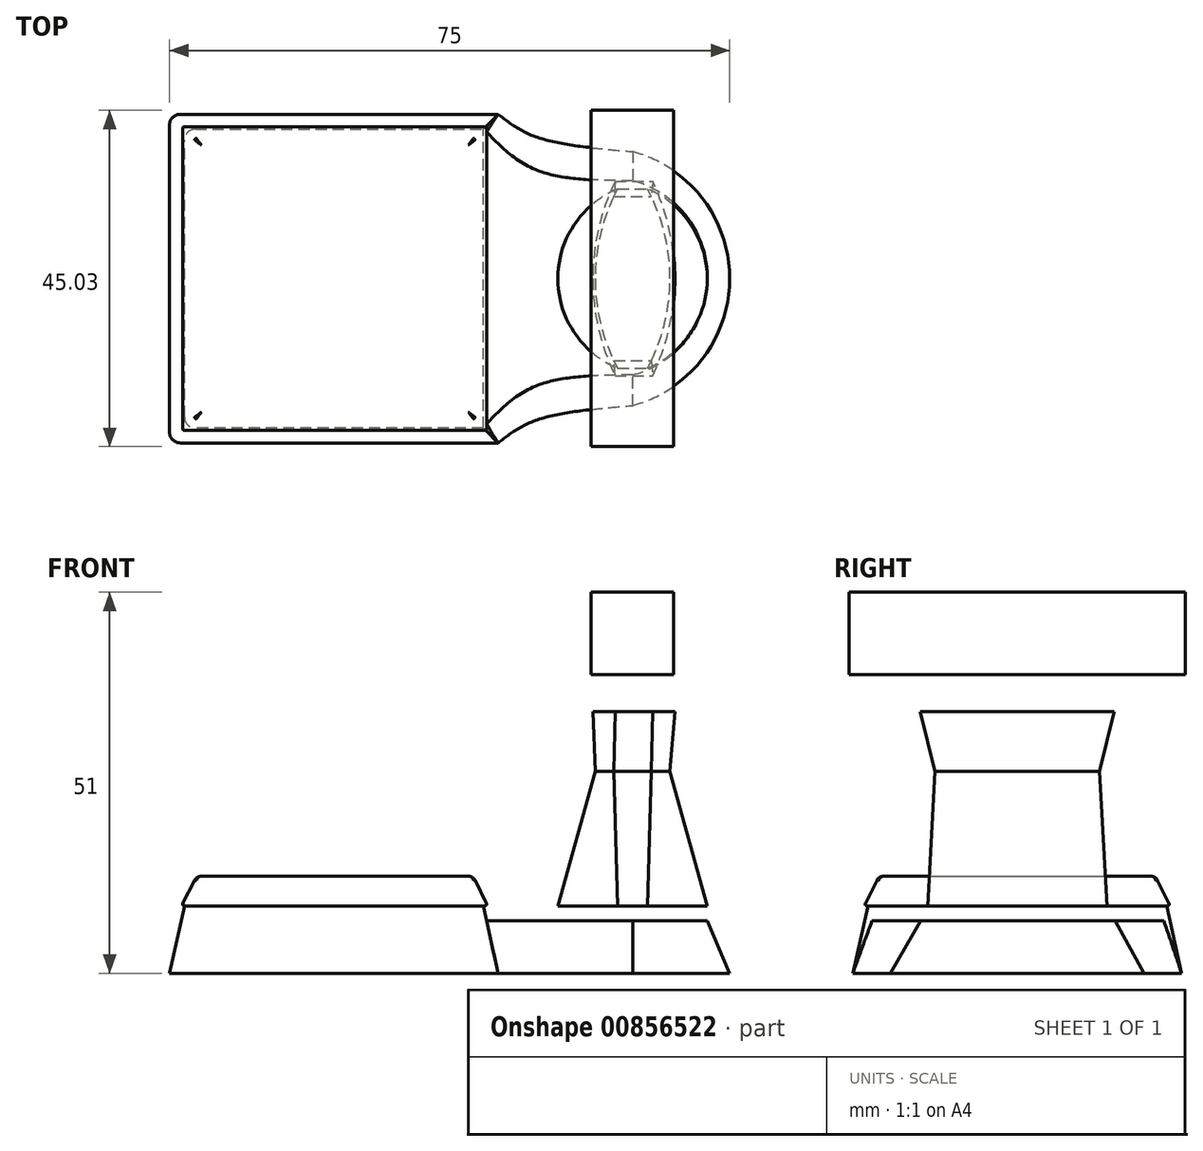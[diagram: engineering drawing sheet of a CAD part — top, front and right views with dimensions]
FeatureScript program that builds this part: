
annotation { "Feature Type Name" : "Feature", "Feature Type Description" : "" }
export const myFeature = defineFeature(function(context is Context, id is Id, definition is map)
    precondition{}
    {
        {
            var Q0;
            Q0=qCreatedBy(makeId("Top.planeOp"),FACE);
            var sketch = newSketch(context, id + "F0", { "sketchPlane" : qUnion([Q0])});
            skLineSegment(sketch, "E0.bottom", {"start": v(0, 0) * mm, "end": v(44, 0) * mm});
            skLineSegment(sketch, "E0.top", {"start": v(0, 44) * mm, "end": v(44, 44) * mm});
            skLineSegment(sketch, "E0.left", {"start": v(0, 0) * mm, "end": v(0, 44) * mm});
            skLineSegment(sketch, "E1", {"start": v(75, 22) * mm, "end": v(62, 22) * mm});
            skLineSegment(sketch, "E2", {"start": v(62, 22) * mm, "end": v(62, 39) * mm});
            skLineSegment(sketch, "E3", {"start": v(62, 22) * mm, "end": v(62, 5) * mm});
            skArc(sketch, "E4", {"start": v(62, 5) * mm, "mid": v(75, 22) * mm, "end": v(62, 39) * mm});
            skFitSpline(sketch, "E5", {"points": [v(44, 44) * mm, v(49, 41) * mm, v(62, 39) * mm], "startDerivative": vector(10.68, -8.34) * mm, "endDerivative": vector(24.4, -2.08) * mm});
            skFitSpline(sketch, "E6", {"points": [v(44, 0) * mm, v(49, 3) * mm, v(62, 5) * mm], "startDerivative": vector(10.68, 8.34) * mm, "endDerivative": vector(24.4, 2.08) * mm});
            skLineSegment(sketch, "E7", {"start": v(44, 0) * mm, "end": v(44, 44) * mm});
            skLineSegment(sketch, "E8", {"start": v(49, 41) * mm, "end": v(49, 3) * mm});
            skSolve(sketch);
        }
        {
            var Q0;
            Q0=qCreatedBy(makeId("Top.planeOp"),FACE);
            cPlane(context, id + "F1", {"entities" : qUnion([Q0]), "cplaneType" : CPlaneType.OFFSET, "offset" : 9 * mm, "width" : 150 * mm, "height" : 150 * mm});
        }
        {
            var Q0;
            Q0=qCreatedBy(id+"F1.planeOp",FACE);
            var sketch = newSketch(context, id + "F2", { "sketchPlane" : qUnion([Q0])});
            skLineSegment(sketch, "E9.top", {"start": v(2, 42) * mm, "end": v(42, 42) * mm});
            skLineSegment(sketch, "E9.left", {"start": v(2, 2) * mm, "end": v(2, 42) * mm});
            skLineSegment(sketch, "E9.right", {"start": v(42, 2) * mm, "end": v(42, 42) * mm});
            skLineSegment(sketch, "E10", {"start": v(62, 22) * mm, "end": v(62, 9) * mm});
            skLineSegment(sketch, "E11", {"start": v(62, 22) * mm, "end": v(72, 22) * mm});
            skLineSegment(sketch, "E12", {"start": v(42, 2) * mm, "end": v(2, 2) * mm});
            skLineSegment(sketch, "E13", {"start": v(49, 36.5) * mm, "end": v(49, 7.5) * mm});
            skLineSegment(sketch, "E14", {"start": v(62, 22) * mm, "end": v(62, 34) * mm});
            skLineSegment(sketch, "E15", {"start": v(62, 22) * mm, "end": v(62, 10) * mm});
            skLineSegment(sketch, "E16", {"start": v(62, 34) * mm, "end": v(64, 34) * mm});
            skLineSegment(sketch, "E17", {"start": v(62, 10) * mm, "end": v(64, 10) * mm});
            skArc(sketch, "E18", {"start": v(64, 10) * mm, "mid": v(72, 22) * mm, "end": v(64, 34) * mm});
            skLineSegment(sketch, "E19", {"start": v(62, 34) * mm, "end": v(60, 34) * mm});
            skLineSegment(sketch, "E20", {"start": v(62, 10) * mm, "end": v(60, 10) * mm});
            skArc(sketch, "E21", {"start": v(60, 34) * mm, "mid": v(52, 22) * mm, "end": v(60, 10) * mm});
            skLineSegment(sketch, "E22", {"start": v(62, 22) * mm, "end": v(52, 22) * mm});
            skSolve(sketch);
        }
        {
            var Q0;
            Q0=makeQuery(id+"F2.imprint","IMPRINT",FACE,{"disambiguationData":[TD([[makeQuery(id+"F2.imprint","IMPRINT",EDGE,{"derivedFrom":sQuery(id+"F2.wireOp",EDGE,"E9.top")}),-1.0]])]});
            var Q1;
            Q1=makeQuery(id+"F0.imprint","IMPRINT",FACE,{"disambiguationData":[TD([[makeQuery(id+"F0.imprint","IMPRINT",EDGE,{"derivedFrom":sQuery(id+"F0.wireOp",EDGE,"E0.bottom")}),1.0]])]});
            loft(context, id + "F3", {"sheetProfilesArray" : [{ "sheetProfileEntities" : qUnion([Q0]) }, { "sheetProfileEntities" : qUnion([Q1]) }]});
        }
        {
            var Q0;
            Q0=makeQuery(id+"F3.opLoft","SWEPT_EDGE",EDGE,{"disambiguationData":[OSD([sQuery(id+"F0.wireOp",EDGE,"E0.bottom"),sQuery(id+"F0.wireOp",EDGE,"E0.left"),sQuery(id+"F2.wireOp",EDGE,"E9.left"),sQuery(id+"F2.wireOp",EDGE,"E12")])]});
            fillet(context, id + "F4", {"entities" : qUnion([Q0]), "radius" : 1.5 * mm, "tangentPropagation" : true, "allowEdgeOverflow" : false});
        }
        {
            var Q0;
            Q0=makeQuery(id+"F3.opLoft","SWEPT_EDGE",EDGE,{"disambiguationData":[OSD([sQuery(id+"F0.wireOp",EDGE,"E0.top"),sQuery(id+"F0.wireOp",EDGE,"E0.left"),sQuery(id+"F2.wireOp",EDGE,"E9.top"),sQuery(id+"F2.wireOp",EDGE,"E9.left")])]});
            fillet(context, id + "F5", {"entities" : qUnion([Q0]), "radius" : 1.5 * mm, "tangentPropagation" : true, "allowEdgeOverflow" : false});
        }
        {
            var Q0;
            Q0=qCreatedBy(id+"F1.planeOp",FACE);
            var sketch = newSketch(context, id + "F6", { "sketchPlane" : qUnion([Q0])});
            skLineSegment(sketch, "E23.bottom", {"start": v(0.1, 0) * mm, "end": v(1.6, 0) * mm});
            skLineSegment(sketch, "E23.top", {"start": v(0.1, 1.5) * mm, "end": v(1.6, 1.5) * mm});
            skLineSegment(sketch, "E23.left", {"start": v(0.1, 0) * mm, "end": v(0.1, 1.5) * mm});
            skLineSegment(sketch, "E23.right", {"start": v(1.6, 0) * mm, "end": v(1.6, 1.5) * mm});
            skLineSegment(sketch, "E24.bottom", {"start": v(1.6, 1.5) * mm, "end": v(42.6, 1.5) * mm});
            skLineSegment(sketch, "E24.top", {"start": v(1.6, 42.5) * mm, "end": v(42.6, 42.5) * mm});
            skLineSegment(sketch, "E24.left", {"start": v(1.6, 1.5) * mm, "end": v(1.6, 42.5) * mm});
            skLineSegment(sketch, "E24.right", {"start": v(42.6, 1.5) * mm, "end": v(42.6, 42.5) * mm});
            skSolve(sketch);
        }
        {
            var Q0;
            Q0=qCreatedBy(id+"F1.planeOp",FACE);
            cPlane(context, id + "F7", {"entities" : qUnion([Q0]), "cplaneType" : CPlaneType.OFFSET, "offset" : 4 * mm, "width" : 150 * mm, "height" : 150 * mm});
        }
        {
            var Q0;
            Q0=qCreatedBy(id+"F7.planeOp",FACE);
            var sketch = newSketch(context, id + "F8", { "sketchPlane" : qUnion([Q0])});
            skLineSegment(sketch, "E25.bottom", {"start": v(0.15, 0) * mm, "end": v(3.65, 0) * mm});
            skLineSegment(sketch, "E25.top", {"start": v(0.15, 3.5) * mm, "end": v(3.65, 3.5) * mm});
            skLineSegment(sketch, "E25.left", {"start": v(0.15, 0) * mm, "end": v(0.15, 3.5) * mm});
            skLineSegment(sketch, "E25.right", {"start": v(3.65, 0) * mm, "end": v(3.65, 3.5) * mm});
            skLineSegment(sketch, "E26.bottom", {"start": v(3.65, 3.5) * mm, "end": v(40.65, 3.5) * mm});
            skLineSegment(sketch, "E26.top", {"start": v(3.65, 40.5) * mm, "end": v(40.65, 40.5) * mm});
            skLineSegment(sketch, "E26.left", {"start": v(3.65, 3.5) * mm, "end": v(3.65, 40.5) * mm});
            skLineSegment(sketch, "E26.right", {"start": v(40.65, 3.5) * mm, "end": v(40.65, 40.5) * mm});
            skSolve(sketch);
        }
        {
            var Q0;
            Q0=makeQuery(id+"F6.imprint","IMPRINT",FACE,{"disambiguationData":[TD([[makeQuery(id+"F6.imprint","IMPRINT",EDGE,{"derivedFrom":sQuery(id+"F6.wireOp",EDGE,"E24.bottom")}),1.0]])]});
            var Q1;
            Q1=makeQuery(id+"F8.imprint","IMPRINT",FACE,{"disambiguationData":[TD([[makeQuery(id+"F8.imprint","IMPRINT",EDGE,{"derivedFrom":sQuery(id+"F8.wireOp",EDGE,"E26.bottom")}),1.0]])]});
            loft(context, id + "F9", {"sheetProfilesArray" : [{ "sheetProfileEntities" : qUnion([Q0]) }, { "sheetProfileEntities" : qUnion([Q1]) }]});
        }
        {
            var Q0;
            Q0=makeQuery(id+"F9.opLoft","MID_CAP_EDGE",EDGE,{"disambiguationData":[OSD([sQuery(id+"F8.wireOp",EDGE,"E25.top"),sQuery(id+"F8.wireOp",EDGE,"E25.right"),sQuery(id+"F8.wireOp",EDGE,"E26.bottom"),sQuery(id+"F8.wireOp",EDGE,"E26.left"),sQuery(id+"F8.wireOp",EDGE,"E26.right")])],"capPos":1.0});
            var Q1;
            Q1=makeQuery(id+"F9.opLoft","MID_CAP_EDGE",EDGE,{"disambiguationData":[OSD([sQuery(id+"F8.wireOp",EDGE,"E25.top"),sQuery(id+"F8.wireOp",EDGE,"E25.right"),sQuery(id+"F8.wireOp",EDGE,"E26.bottom"),sQuery(id+"F8.wireOp",EDGE,"E26.top"),sQuery(id+"F8.wireOp",EDGE,"E26.left")])],"capPos":1.0});
            var Q2;
            Q2=makeQuery(id+"F9.opLoft","CAP_FACE",FACE,{"disambiguationData":[OSD([makeQuery(id+"F8.imprint","IMPRINT",FACE,{"disambiguationData":[TD([[makeQuery(id+"F8.imprint","IMPRINT",EDGE,{"derivedFrom":sQuery(id+"F8.wireOp",EDGE,"E26.bottom")}),1.0]])]})])],"isStart":true});
            fillet(context, id + "F10", {"entities" : qUnion([Q0, Q1, Q2]), "radius" : 1 * mm, "tangentPropagation" : true, "allowEdgeOverflow" : false});
        }
        {
            var Q0;
            Q0=makeQuery(id+"F9.opLoft","SWEPT_FACE",FACE,{"disambiguationData":[OSD([sQuery(id+"F6.wireOp",EDGE,"E23.top"),sQuery(id+"F6.wireOp",EDGE,"E23.right"),sQuery(id+"F6.wireOp",EDGE,"E24.bottom"),sQuery(id+"F6.wireOp",EDGE,"E24.left"),sQuery(id+"F6.wireOp",EDGE,"E24.right"),sQuery(id+"F8.wireOp",EDGE,"E25.top"),sQuery(id+"F8.wireOp",EDGE,"E25.right"),sQuery(id+"F8.wireOp",EDGE,"E26.bottom"),sQuery(id+"F8.wireOp",EDGE,"E26.left"),sQuery(id+"F8.wireOp",EDGE,"E26.right")])]});
            var Q1;
            Q1=makeQuery(id+"F9.opLoft","SWEPT_FACE",FACE,{"disambiguationData":[OSD([sQuery(id+"F6.wireOp",EDGE,"E23.top"),sQuery(id+"F6.wireOp",EDGE,"E23.right"),sQuery(id+"F6.wireOp",EDGE,"E24.bottom"),sQuery(id+"F6.wireOp",EDGE,"E24.top"),sQuery(id+"F6.wireOp",EDGE,"E24.left"),sQuery(id+"F8.wireOp",EDGE,"E25.top"),sQuery(id+"F8.wireOp",EDGE,"E25.right"),sQuery(id+"F8.wireOp",EDGE,"E26.bottom"),sQuery(id+"F8.wireOp",EDGE,"E26.top"),sQuery(id+"F8.wireOp",EDGE,"E26.left")])]});
            var Q2;
            Q2=makeQuery(id+"F9.opLoft","SWEPT_FACE",FACE,{"disambiguationData":[OSD([sQuery(id+"F6.wireOp",EDGE,"E24.bottom"),sQuery(id+"F6.wireOp",EDGE,"E24.top"),sQuery(id+"F6.wireOp",EDGE,"E24.right"),sQuery(id+"F8.wireOp",EDGE,"E26.bottom"),sQuery(id+"F8.wireOp",EDGE,"E26.top"),sQuery(id+"F8.wireOp",EDGE,"E26.right")])]});
            var Q3;
            Q3=makeQuery(id+"F9.opLoft","SWEPT_FACE",FACE,{"disambiguationData":[OSD([sQuery(id+"F6.wireOp",EDGE,"E24.top"),sQuery(id+"F6.wireOp",EDGE,"E24.left"),sQuery(id+"F6.wireOp",EDGE,"E24.right"),sQuery(id+"F8.wireOp",EDGE,"E26.top"),sQuery(id+"F8.wireOp",EDGE,"E26.left"),sQuery(id+"F8.wireOp",EDGE,"E26.right")])]});
            fillet(context, id + "F11", {"entities" : qUnion([Q0, Q1, Q2, Q3]), "radius" : 0.25 * mm, "tangentPropagation" : true, "allowEdgeOverflow" : false});
        }
        {
            var Q0;
            Q0=qCreatedBy(makeId("Top.planeOp"),FACE);
            cPlane(context, id + "F12", {"entities" : qUnion([Q0]), "cplaneType" : CPlaneType.OFFSET, "offset" : 40 * mm, "width" : 150 * mm, "height" : 150 * mm});
        }
        {
            var Q0;
            Q0=qCreatedBy(id+"F12.planeOp",FACE);
            var sketch = newSketch(context, id + "F13", { "sketchPlane" : qUnion([Q0])});
            skLineSegment(sketch, "E27.bottom", {"start": v(56.47, 44.53) * mm, "end": v(67.47, 44.53) * mm});
            skLineSegment(sketch, "E27.top", {"start": v(56.47, -0.5) * mm, "end": v(67.47, -0.5) * mm});
            skLineSegment(sketch, "E28", {"start": v(56.47, 44.53) * mm, "end": v(56.47, -0.5) * mm});
            skLineSegment(sketch, "E29", {"start": v(67.47, 44.53) * mm, "end": v(67.47, -0.5) * mm});
            skSolve(sketch);
        }
        {
            var Q0;
            Q0=makeQuery(id+"F13.imprint","IMPRINT",FACE,{"disambiguationData":[TD([[makeQuery(id+"F13.imprint","IMPRINT",EDGE,{"derivedFrom":sQuery(id+"F13.wireOp",EDGE,"E27.bottom")}),-1.0]])]});
            extrude(context, id + "F14", {"entities" : qUnion([Q0]), "depth" : 11 * mm, "offsetDistance" : 25 * mm});
        }
        {
            var Q0;
            Q0=qCreatedBy(makeId("Top.planeOp"),FACE);
            cPlane(context, id + "F15", {"entities" : qUnion([Q0]), "cplaneType" : CPlaneType.OFFSET, "offset" : 27 * mm, "width" : 150 * mm, "height" : 150 * mm});
        }
        {
            var Q0;
            Q0=qCreatedBy(makeId("Top.planeOp"),FACE);
            cPlane(context, id + "F16", {"entities" : qUnion([Q0]), "cplaneType" : CPlaneType.OFFSET, "offset" : 35 * mm, "width" : 150 * mm, "height" : 150 * mm});
        }
        {
            var Q0;
            Q0=qCreatedBy(id+"F15.planeOp",FACE);
            var sketch = newSketch(context, id + "F17", { "sketchPlane" : qUnion([Q0])});
            skLineSegment(sketch, "E30", {"start": v(67, 22) * mm, "end": v(62, 22) * mm});
            skLineSegment(sketch, "E31", {"start": v(62, 22) * mm, "end": v(62, 33) * mm});
            skLineSegment(sketch, "E32", {"start": v(62, 22) * mm, "end": v(62, 11) * mm});
            skLineSegment(sketch, "E33", {"start": v(62, 22) * mm, "end": v(57, 22) * mm});
            skLineSegment(sketch, "E34", {"start": v(62, 33) * mm, "end": v(64.5, 33) * mm});
            skLineSegment(sketch, "E35", {"start": v(62, 33) * mm, "end": v(59.5, 33) * mm});
            skLineSegment(sketch, "E36", {"start": v(62, 11) * mm, "end": v(64.5, 11) * mm});
            skLineSegment(sketch, "E37", {"start": v(62, 11) * mm, "end": v(59.5, 11) * mm});
            skArc(sketch, "E38", {"start": v(64.5, 11) * mm, "mid": v(67, 22) * mm, "end": v(64.5, 33) * mm});
            skArc(sketch, "E39", {"start": v(59.5, 33) * mm, "mid": v(57, 22) * mm, "end": v(59.5, 11) * mm});
            skSolve(sketch);
        }
        {
            var Q0;
            Q0=qCreatedBy(id+"F16.planeOp",FACE);
            var sketch = newSketch(context, id + "F18", { "sketchPlane" : qUnion([Q0])});
            skLineSegment(sketch, "E40", {"start": v(62.17, 22) * mm, "end": v(62.17, 35) * mm});
            skLineSegment(sketch, "E41", {"start": v(62.17, 22) * mm, "end": v(62.17, 9) * mm});
            skLineSegment(sketch, "E42", {"start": v(62.17, 35) * mm, "end": v(64.67, 35) * mm});
            skLineSegment(sketch, "E43", {"start": v(62.17, 35) * mm, "end": v(59.67, 35) * mm});
            skLineSegment(sketch, "E44", {"start": v(62.17, 9) * mm, "end": v(64.67, 9) * mm});
            skLineSegment(sketch, "E45", {"start": v(62.17, 9) * mm, "end": v(59.67, 9) * mm});
            skLineSegment(sketch, "E46", {"start": v(62.17, 22) * mm, "end": v(67.67, 22) * mm});
            skLineSegment(sketch, "E47", {"start": v(67.67, 22) * mm, "end": v(62.17, 22) * mm});
            skLineSegment(sketch, "E48", {"start": v(62.17, 22) * mm, "end": v(56.67, 22) * mm});
            skArc(sketch, "E49", {"start": v(64.67, 9) * mm, "mid": v(67.67, 22) * mm, "end": v(64.67, 35) * mm});
            skArc(sketch, "E50", {"start": v(59.67, 35) * mm, "mid": v(56.67, 22) * mm, "end": v(59.67, 9) * mm});
            skSolve(sketch);
        }
        {
            var Q0;
            Q0=qCreatedBy(makeId("Top.planeOp"),FACE);
            cPlane(context, id + "F19", {"entities" : qUnion([Q0]), "cplaneType" : CPlaneType.OFFSET, "offset" : 7 * mm, "width" : 150 * mm, "height" : 150 * mm});
        }
        {
            var Q0;
            Q0=qCreatedBy(id+"F19.planeOp",FACE);
            var sketch = newSketch(context, id + "F20", { "sketchPlane" : qUnion([Q0])});
            skLineSegment(sketch, "E51.top", {"start": v(2, 42.1) * mm, "end": v(42, 42.1) * mm});
            skLineSegment(sketch, "E51.left", {"start": v(2, 2.1) * mm, "end": v(2, 42.1) * mm});
            skLineSegment(sketch, "E51.right", {"start": v(42, 2.1) * mm, "end": v(42, 42.1) * mm});
            skLineSegment(sketch, "E52", {"start": v(62, 22.1) * mm, "end": v(62, 35.1) * mm});
            skLineSegment(sketch, "E53", {"start": v(62, 22.1) * mm, "end": v(62, 9.1) * mm});
            skLineSegment(sketch, "E54", {"start": v(62, 22.1) * mm, "end": v(72, 22.1) * mm});
            skArc(sketch, "E55", {"start": v(62, 9.1) * mm, "mid": v(72, 22.1) * mm, "end": v(62, 35.1) * mm});
            skLineSegment(sketch, "E56", {"start": v(42, 2.1) * mm, "end": v(2, 2.1) * mm});
            skLineSegment(sketch, "E57", {"start": v(49, 36.6) * mm, "end": v(49, 7.6) * mm});
            skFitSpline(sketch, "E58", {"points": [v(62, 35.1) * mm, v(49, 36.6) * mm, v(42, 42.1) * mm], "startDerivative": vector(-25.98, 0.15) * mm, "endDerivative": vector(-13.63, 14.3) * mm});
            skFitSpline(sketch, "E59", {"points": [v(62, 9.1) * mm, v(49, 7.6) * mm, v(42, 2.1) * mm], "startDerivative": vector(-25.98, -0.15) * mm, "endDerivative": vector(-13.63, -14.3) * mm});
            skSolve(sketch);
        }
        {
            var Q0;
            {var subQ0=sQuery(id+"F17.wireOp",EDGE,"E30");Q0=makeQuery(id+"F17.imprint","IMPRINT",FACE,{"disambiguationData":[TD([[makeQuery(id+"F17.imprint","IMPRINT",EDGE,{"derivedFrom":subQ0}),1.0]])]});}
            var Q1;
            Q1=makeQuery(id+"F18.imprint","IMPRINT",FACE,{"disambiguationData":[TD([[makeQuery(id+"F18.imprint","IMPRINT",EDGE,{"derivedFrom":sQuery(id+"F18.wireOp",EDGE,"E41")}),1.0]])]});
            loft(context, id + "F21", {"sheetProfilesArray" : [{ "sheetProfileEntities" : qUnion([Q0]) }, { "sheetProfileEntities" : qUnion([Q1]) }]});
        }
        {
            var Q1;
            Q1=makeQuery(id+"F18.imprint","IMPRINT",FACE,{"disambiguationData":[TD([[makeQuery(id+"F18.imprint","IMPRINT",EDGE,{"derivedFrom":sQuery(id+"F18.wireOp",EDGE,"E40")}),-1.0]])]});
            var Q2;
            {var subQ0=sQuery(id+"F17.wireOp",EDGE,"E30");Q2=makeQuery(id+"F17.imprint","IMPRINT",FACE,{"disambiguationData":[TD([[makeQuery(id+"F17.imprint","IMPRINT",EDGE,{"derivedFrom":subQ0}),-1.0]])]});}
            loft(context, id + "F22", {"operationType" : NewBodyOperationType.ADD, "sheetProfilesArray" : [{ "sheetProfileEntities" : qUnion([Q1]) }, { "sheetProfileEntities" : qUnion([Q2]) }]});
        }
        {
            var Q1;
            Q1=makeQuery(id+"F18.imprint","IMPRINT",FACE,{"disambiguationData":[TD([[makeQuery(id+"F18.imprint","IMPRINT",EDGE,{"derivedFrom":sQuery(id+"F18.wireOp",EDGE,"E40")}),1.0]])]});
            var Q2;
            Q2=makeQuery(id+"F17.imprint","IMPRINT",FACE,{"disambiguationData":[TD([[makeQuery(id+"F17.imprint","IMPRINT",EDGE,{"derivedFrom":sQuery(id+"F17.wireOp",EDGE,"E31")}),1.0]])]});
            loft(context, id + "F23", {"operationType" : NewBodyOperationType.ADD, "sheetProfilesArray" : [{ "sheetProfileEntities" : qUnion([Q1]) }, { "sheetProfileEntities" : qUnion([Q2]) }]});
        }
        {
            var Q1;
            Q1=makeQuery(id+"F18.imprint","IMPRINT",FACE,{"disambiguationData":[TD([[makeQuery(id+"F18.imprint","IMPRINT",EDGE,{"derivedFrom":sQuery(id+"F18.wireOp",EDGE,"E41")}),-1.0]])]});
            var Q2;
            Q2=makeQuery(id+"F17.imprint","IMPRINT",FACE,{"disambiguationData":[TD([[makeQuery(id+"F17.imprint","IMPRINT",EDGE,{"derivedFrom":sQuery(id+"F17.wireOp",EDGE,"E32")}),-1.0]])]});
            loft(context, id + "F24", {"operationType" : NewBodyOperationType.ADD, "sheetProfilesArray" : [{ "sheetProfileEntities" : qUnion([Q1]) }, { "sheetProfileEntities" : qUnion([Q2]) }]});
        }
        {
            var Q1;
            {var subQ0=sQuery(id+"F17.wireOp",EDGE,"E30");Q1=makeQuery(id+"F17.imprint","IMPRINT",FACE,{"disambiguationData":[TD([[makeQuery(id+"F17.imprint","IMPRINT",EDGE,{"derivedFrom":subQ0}),-1.0]])]});}
            var Q2;
            {var subQ0=sQuery(id+"F2.wireOp",EDGE,"E11");Q2=makeQuery(id+"F2.imprint","IMPRINT",FACE,{"disambiguationData":[TD([[makeQuery(id+"F2.imprint","IMPRINT",EDGE,{"derivedFrom":subQ0}),1.0]])]});}
            loft(context, id + "F25", {"operationType" : NewBodyOperationType.ADD, "sheetProfilesArray" : [{ "sheetProfileEntities" : qUnion([Q1]) }, { "sheetProfileEntities" : qUnion([Q2]) }]});
        }
        {
            var Q1;
            {var subQ0=sQuery(id+"F2.wireOp",EDGE,"E11");Q1=makeQuery(id+"F2.imprint","IMPRINT",FACE,{"disambiguationData":[TD([[makeQuery(id+"F2.imprint","IMPRINT",EDGE,{"derivedFrom":subQ0}),-1.0]])]});}
            var Q2;
            {var subQ0=sQuery(id+"F17.wireOp",EDGE,"E30");Q2=makeQuery(id+"F17.imprint","IMPRINT",FACE,{"disambiguationData":[TD([[makeQuery(id+"F17.imprint","IMPRINT",EDGE,{"derivedFrom":subQ0}),1.0]])]});}
            loft(context, id + "F26", {"operationType" : NewBodyOperationType.ADD, "sheetProfilesArray" : [{ "sheetProfileEntities" : qUnion([Q1]) }, { "sheetProfileEntities" : qUnion([Q2]) }]});
        }
        {
            var Q1;
            Q1=makeQuery(id+"F17.imprint","IMPRINT",FACE,{"disambiguationData":[TD([[makeQuery(id+"F17.imprint","IMPRINT",EDGE,{"derivedFrom":sQuery(id+"F17.wireOp",EDGE,"E31")}),1.0]])]});
            var Q2;
            Q2=makeQuery(id+"F2.imprint","IMPRINT",FACE,{"disambiguationData":[TD([[makeQuery(id+"F2.imprint","IMPRINT",EDGE,{"derivedFrom":sQuery(id+"F2.wireOp",EDGE,"E14")}),1.0]])]});
            loft(context, id + "F27", {"operationType" : NewBodyOperationType.ADD, "sheetProfilesArray" : [{ "sheetProfileEntities" : qUnion([Q1]) }, { "sheetProfileEntities" : qUnion([Q2]) }]});
        }
        {
            var Q1;
            Q1=makeQuery(id+"F17.imprint","IMPRINT",FACE,{"disambiguationData":[TD([[makeQuery(id+"F17.imprint","IMPRINT",EDGE,{"derivedFrom":sQuery(id+"F17.wireOp",EDGE,"E32")}),-1.0]])]});
            var Q2;
            {var subQ2=sQuery(id+"F2.wireOp",EDGE,"E20");Q2=makeQuery(id+"F2.imprint","IMPRINT",FACE,{"disambiguationData":[TD([[makeQuery(id+"F2.imprint","IMPRINT",EDGE,{"derivedFrom":subQ2}),-1.0]])]});}
            loft(context, id + "F28", {"operationType" : NewBodyOperationType.ADD, "sheetProfilesArray" : [{ "sheetProfileEntities" : qUnion([Q1]) }, { "sheetProfileEntities" : qUnion([Q2]) }]});
        }
        {
            var Q1;
            {var subQ0=sQuery(id+"F20.wireOp",EDGE,"E51.right");Q1=makeQuery(id+"F20.imprint","IMPRINT",FACE,{"disambiguationData":[TD([[makeQuery(id+"F20.imprint","IMPRINT",EDGE,{"derivedFrom":subQ0}),-1.0]])]});}
            var Q2;
            {var subQ0=sQuery(id+"F0.wireOp",EDGE,"E7");Q2=makeQuery(id+"F0.imprint","IMPRINT",FACE,{"disambiguationData":[TD([[makeQuery(id+"F0.imprint","IMPRINT",EDGE,{"derivedFrom":subQ0}),-1.0]])]});}
            loft(context, id + "F29", {"operationType" : NewBodyOperationType.ADD, "sheetProfilesArray" : [{ "sheetProfileEntities" : qUnion([Q1]) }, { "sheetProfileEntities" : qUnion([Q2]) }]});
        }
        {
            var Q1;
            {var subQ5=sQuery(id+"F0.wireOp",EDGE,"E2");Q1=makeQuery(id+"F0.imprint","IMPRINT",FACE,{"disambiguationData":[TD([[makeQuery(id+"F0.imprint","IMPRINT",EDGE,{"derivedFrom":subQ5}),1.0]])]});}
            var Q2;
            {var subQ2=sQuery(id+"F20.wireOp",EDGE,"E52");Q2=makeQuery(id+"F20.imprint","IMPRINT",FACE,{"disambiguationData":[TD([[makeQuery(id+"F20.imprint","IMPRINT",EDGE,{"derivedFrom":subQ2}),1.0]])]});}
            loft(context, id + "F30", {"operationType" : NewBodyOperationType.ADD, "sheetProfilesArray" : [{ "sheetProfileEntities" : qUnion([Q1]) }, { "sheetProfileEntities" : qUnion([Q2]) }]});
        }
        {
            var Q1;
            {var subQ0=sQuery(id+"F0.wireOp",EDGE,"E1");Q1=makeQuery(id+"F0.imprint","IMPRINT",FACE,{"disambiguationData":[TD([[makeQuery(id+"F0.imprint","IMPRINT",EDGE,{"derivedFrom":subQ0}),-1.0]])]});}
            var Q2;
            {var subQ0=sQuery(id+"F20.wireOp",EDGE,"E52");Q2=makeQuery(id+"F20.imprint","IMPRINT",FACE,{"disambiguationData":[TD([[makeQuery(id+"F20.imprint","IMPRINT",EDGE,{"derivedFrom":subQ0}),-1.0]])]});}
            loft(context, id + "F31", {"operationType" : NewBodyOperationType.ADD, "sheetProfilesArray" : [{ "sheetProfileEntities" : qUnion([Q1]) }, { "sheetProfileEntities" : qUnion([Q2]) }]});
        }
        {
            var Q1;
            {var subQ0=sQuery(id+"F20.wireOp",EDGE,"E53");Q1=makeQuery(id+"F20.imprint","IMPRINT",FACE,{"disambiguationData":[TD([[makeQuery(id+"F20.imprint","IMPRINT",EDGE,{"derivedFrom":subQ0}),1.0]])]});}
            var Q2;
            {var subQ0=sQuery(id+"F0.wireOp",EDGE,"E1");Q2=makeQuery(id+"F0.imprint","IMPRINT",FACE,{"disambiguationData":[TD([[makeQuery(id+"F0.imprint","IMPRINT",EDGE,{"derivedFrom":subQ0}),1.0]])]});}
            loft(context, id + "F32", {"operationType" : NewBodyOperationType.ADD, "sheetProfilesArray" : [{ "sheetProfileEntities" : qUnion([Q1]) }, { "sheetProfileEntities" : qUnion([Q2]) }]});
        }
    });
